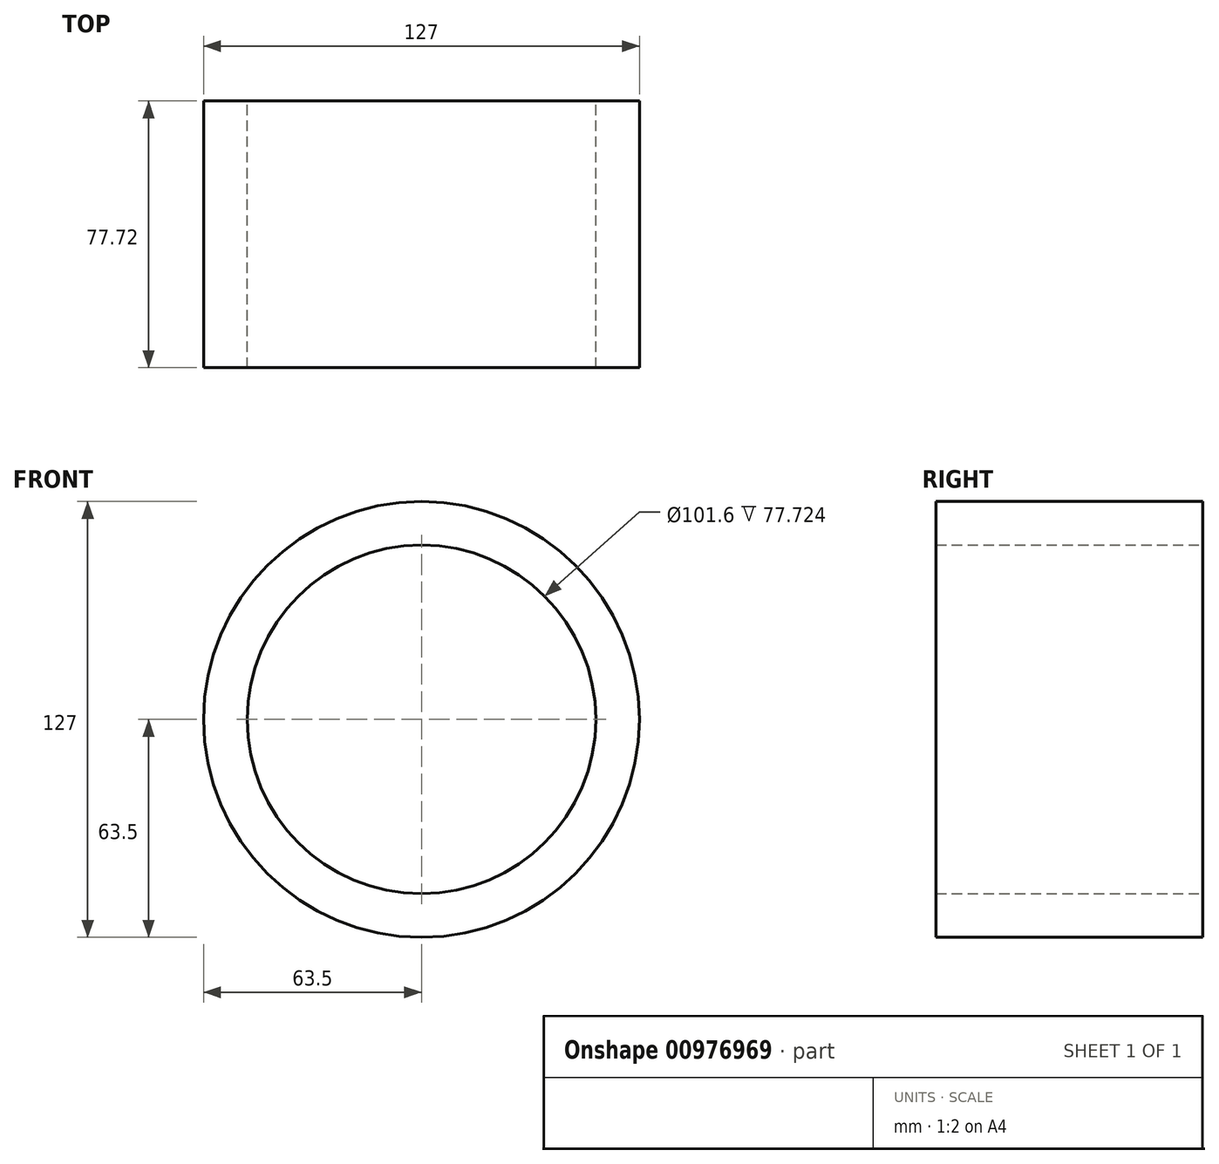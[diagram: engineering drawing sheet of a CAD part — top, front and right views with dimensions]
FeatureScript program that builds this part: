
annotation { "Feature Type Name" : "Feature", "Feature Type Description" : "" }
export const myFeature = defineFeature(function(context is Context, id is Id, definition is map)
    precondition{}
    {
        {
            var Q0;
            Q0=qCreatedBy(makeId("Front.planeOp"),FACE);
            var sketch = newSketch(context, id + "F0", { "sketchPlane" : qUnion([Q0])});
            skCircle(sketch, "E0", {"center": v(0, 0) * mm, "radius": 50.8 * mm});
            skCircle(sketch, "E1", {"center": v(0, 0) * mm, "radius": 63.5 * mm});
            skSolve(sketch);
        }
        {
            var Q0;
            Q0 = qSketchRegion(id + "F0", true);
            var Q1;
            Q1 = qSketchRegion(id + "F2", true);
            extrude(context, id + "F1", {"entities" : qUnion([Q0, Q1]), "depth" : 77.72 * mm, "offsetDistance" : 25.4 * mm});
        }
    });
